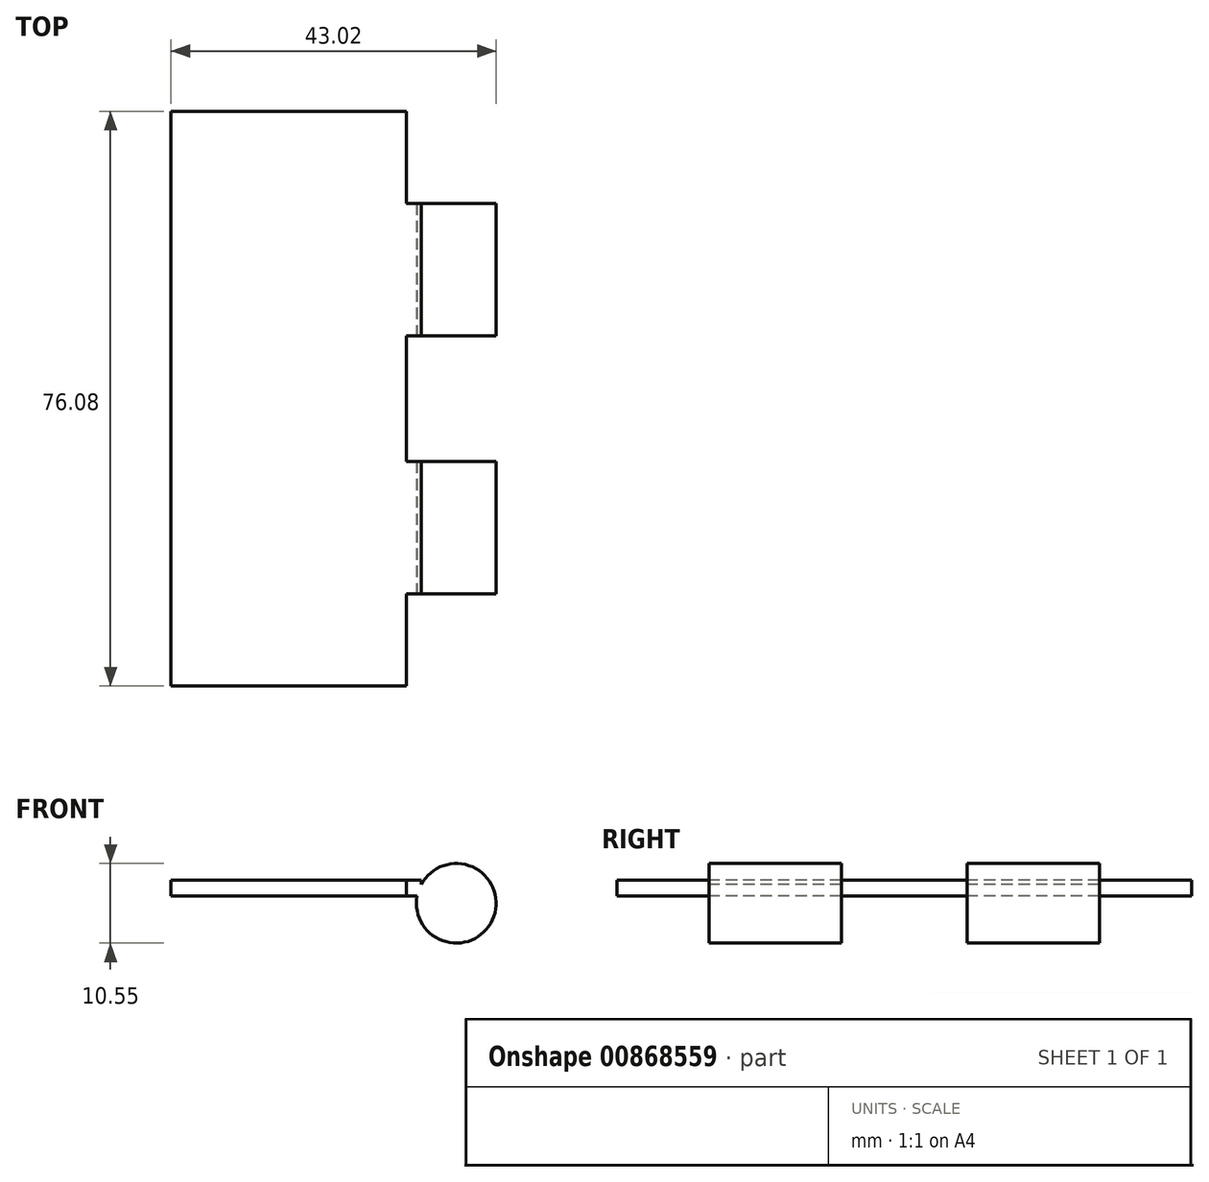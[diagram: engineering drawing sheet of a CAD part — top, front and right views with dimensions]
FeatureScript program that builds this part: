
annotation { "Feature Type Name" : "Feature", "Feature Type Description" : "" }
export const myFeature = defineFeature(function(context is Context, id is Id, definition is map)
    precondition{}
    {
        {
            var Q0;
            Q0=qCreatedBy(makeId("Top.planeOp"),FACE);
            var sketch = newSketch(context, id + "F0", { "sketchPlane" : qUnion([Q0])});
            skLineSegment(sketch, "E0.bottom", {"start": v(15.58, 38.04) * mm, "end": v(-15.58, 38.04) * mm});
            skLineSegment(sketch, "E0.top", {"start": v(15.58, -38.04) * mm, "end": v(-15.58, -38.04) * mm});
            skLineSegment(sketch, "E0.left", {"start": v(15.58, 38.04) * mm, "end": v(15.58, -38.04) * mm});
            skLineSegment(sketch, "E0.right", {"start": v(-15.58, 38.04) * mm, "end": v(-15.58, -38.04) * mm});
            skPoint(sketch, "E0.middle", {"position": v(0, 0) * mm});
            skSolve(sketch);
        }
        {
            var Q0;
            Q0 = qSketchRegion(id + "F0", true);
            extrude(context, id + "F1", {"entities" : qUnion([Q0]), "depth" : 2.1 * mm, "offsetDistance" : 25.4 * mm});
        }
        {
            var Q0;
            Q0=makeQuery(id+"F1.opExtrude","SWEPT_FACE",FACE,{"disambiguationData":[OSD([sQuery(id+"F0.wireOp",EDGE,"E0.left")])]});
            var sketch = newSketch(context, id + "F2", { "sketchPlane" : qUnion([Q0])});
            skLineSegment(sketch, "E1.bottom", {"start": v(-25.84, 2.1) * mm, "end": v(-8.32, 2.1) * mm});
            skLineSegment(sketch, "E1.top", {"start": v(-25.84, 0) * mm, "end": v(-8.32, 0) * mm});
            skLineSegment(sketch, "E1.left", {"start": v(-25.84, 2.1) * mm, "end": v(-25.84, 0) * mm});
            skLineSegment(sketch, "E1.right", {"start": v(-8.32, 2.1) * mm, "end": v(-8.32, 0) * mm});
            skLineSegment(sketch, "E2.bottom", {"start": v(8.32, 2.1) * mm, "end": v(25.84, 2.1) * mm});
            skLineSegment(sketch, "E2.top", {"start": v(8.32, 0) * mm, "end": v(25.84, 0) * mm});
            skLineSegment(sketch, "E2.left", {"start": v(8.32, 2.1) * mm, "end": v(8.32, 0) * mm});
            skLineSegment(sketch, "E2.right", {"start": v(25.84, 2.1) * mm, "end": v(25.84, 0) * mm});
            skSolve(sketch);
        }
        {
            var Q0;
            Q0 = qSketchRegion(id + "F2", true);
            extrude(context, id + "F3", {"entities" : qUnion([Q0]), "operationType" : NewBodyOperationType.ADD, "depth" : 1.96 * mm, "offsetDistance" : 25.4 * mm});
        }
        {
            var Q0;
            Q0=makeQuery(id+"F3.opExtrude","SWEPT_FACE",FACE,{"disambiguationData":[OSD([sQuery(id+"F2.wireOp",EDGE,"E1.left")])]});
            var sketch = newSketch(context, id + "F4", { "sketchPlane" : qUnion([Q0])});
            skCircle(sketch, "E3", {"center": v(22.17, -0.97) * mm, "radius": 5.27 * mm});
            skPoint(sketch, "E4", {"position": v(22.17, 4.3) * mm});
            skPoint(sketch, "E5", {"position": v(27.44, -0.97) * mm});
            skSolve(sketch);
        }
        {
            var Q0;
            Q0 = qSketchRegion(id + "F4", true);
            var Q1;
            Q1=makeQuery(id+"F3.opExtrude","SWEPT_FACE",FACE,{"disambiguationData":[OSD([sQuery(id+"F2.wireOp",EDGE,"E1.right")])]});
            extrude(context, id + "F5", {"entities" : qUnion([Q0]), "operationType" : NewBodyOperationType.ADD, "endBound" : BoundingType.UP_TO_SURFACE, "oppositeDirection" : true, "depth" : 25.4 * mm, "endBoundEntityFace" : qUnion([Q1]), "offsetDistance" : 25.4 * mm});
        }
        {
            var Q0;
            Q0=makeQuery(id+"F3.opExtrude","SWEPT_FACE",FACE,{"disambiguationData":[OSD([sQuery(id+"F2.wireOp",EDGE,"E2.left")])]});
            var sketch = newSketch(context, id + "F6", { "sketchPlane" : qUnion([Q0])});
            skArc(sketch, "E6.0", {"start": v(17, 0) * mm, "mid": v(27.14, -2.72) * mm, "end": v(17.54, 1.54) * mm});
            skLineSegment(sketch, "E7.0", {"start": v(17.54, 0) * mm, "end": v(17, 0) * mm});
            skLineSegment(sketch, "E8.0", {"start": v(17.54, 1.54) * mm, "end": v(17.54, 0) * mm});
            skPoint(sketch, "E9.orphan", {"position": v(15.58, 0) * mm});
            skPoint(sketch, "E10.orphan", {"position": v(17.54, 2.1) * mm});
            skSolve(sketch);
        }
        {
            var Q0;
            Q0 = qSketchRegion(id + "F6", true);
            var Q1;
            Q1=makeQuery(id+"F3.opExtrude","SWEPT_FACE",FACE,{"disambiguationData":[OSD([sQuery(id+"F2.wireOp",EDGE,"E2.right")])]});
            extrude(context, id + "F7", {"entities" : qUnion([Q0]), "operationType" : NewBodyOperationType.ADD, "endBound" : BoundingType.UP_TO_SURFACE, "oppositeDirection" : true, "depth" : 25.4 * mm, "endBoundEntityFace" : qUnion([Q1]), "offsetDistance" : 25.4 * mm});
        }
    });
